# Revit family: Closet_Support_0230_JRSmith
name_source: partatom
category: Plumbing Fixtures
revit_build: Autodesk Revit MEP 2012 (Build: 20110309_2315(x64)
units: mm (PartAtom-declared; Revit-internal decimal feet)

## types (3) — shared parameters
04 CSI = 22 05 29
95 CSI = 15050
Assembly Code = D2010110
Barrel Height = 23"
Capacity = 300lb
Caulk Connection = Yes
Closet Outlet Gasket Radius = 2"
Default Elevation = 0"
Description = Adjustable Fixture Support for Siphon Jet Water Closet
Fixture Offset = 0"
Inlet Pipe Offset = 4"
Inner Offset = 1 1/2"
LEED = Yes
Manufacturer = Jay R. Smith Mfg. Co.
Material = Cast Iron
Material Finish = Duco coated
Model = 0230Y
No-Hub Connection = Yes
Offset From Base = 9"
OmniClass Code = 22-22 42 13
OmniClass Title = Commercial Water Closets, Urinals, and Bidets
Product URL = http://www.jrsmith.com
R = 2"
Rear Pipe Length = 11 1/2"
SMARTBIM Object Version = 3
SMARTBIM URL = www.smartbim.com
Technical and Installation = http://www.jrsmith.com
Top Inlet = 6 21/256"
Top of Rear Pipe Height = 11 1/2"
Type Comments = 0230Y
URL = http://www.jrsmith.com
Vent Pipe Height = 16 183/256"
Warranty = 1 year material and workmanship
zero-valued in all types: Max.Static Load Lbs

## per-type parameters (varying)
| type | Barrel Width | C | E | Nipple Length | Pipe Diameter | Pipe Radius | Stud Length | Weight (lb) |
| 0230Y-4 | 6 1/2" | 9" | 14" | 8" | 4 1/2" | 2 1/4" | 7" | 101 |
| 0230Y-5 | 6" | 11 1/2" | 11 1/2" | 9" | 5 1/2" | 2 3/4" | 9" | 100 |
| 0230Y-6 | 6 1/2" | 11 1/2" | 11 1/2" | 9" | 6 1/2" | 3 1/4" | 9" | 101 |

## geometry (parser evidence)
native form markers: Blend x10, Sweep x20
no freeform markers — native parametric forms only
